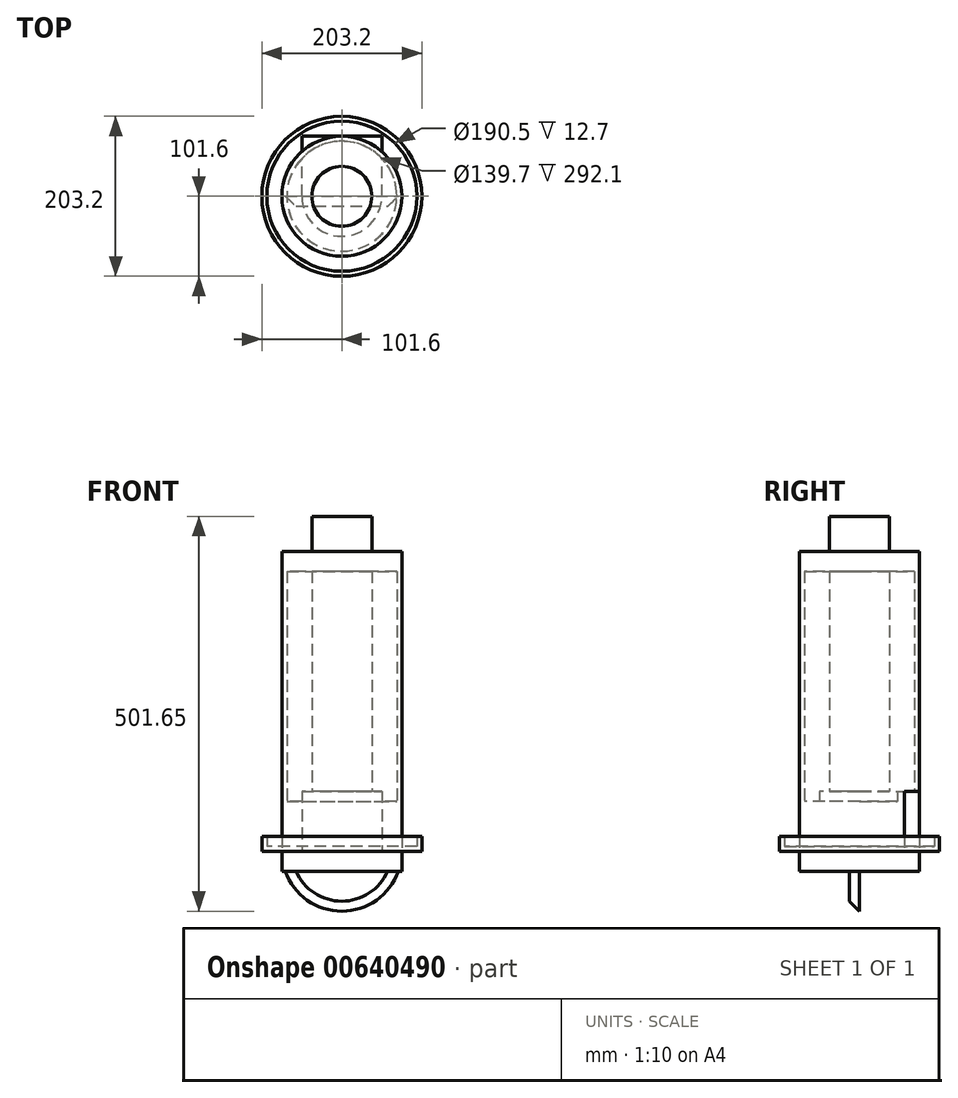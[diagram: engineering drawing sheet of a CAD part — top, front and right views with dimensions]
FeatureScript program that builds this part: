
annotation { "Feature Type Name" : "Feature", "Feature Type Description" : "" }
export const myFeature = defineFeature(function(context is Context, id is Id, definition is map)
    precondition{}
    {
        {
            var Q0;
            Q0=qCreatedBy(makeId("Top.planeOp"),FACE);
            var sketch = newSketch(context, id + "F0", { "sketchPlane" : qUnion([Q0])});
            skArc(sketch, "E0", {"start": v(-50.8, 0) * mm, "mid": v(0, -50.8) * mm, "end": v(50.8, 0) * mm});
            skCircle(sketch, "E1", {"center": v(0, 0) * mm, "radius": 25.4 * mm});
            skLineSegment(sketch, "E2", {"start": v(-50.8, 0) * mm, "end": v(50.8, 0) * mm});
            skLineSegment(sketch, "E3", {"start": v(50.8, 0) * mm, "end": v(50.8, 76.2) * mm});
            skLineSegment(sketch, "E4", {"start": v(-50.8, 0) * mm, "end": v(-50.8, 76.2) * mm});
            skLineSegment(sketch, "E5", {"start": v(-50.8, 76.2) * mm, "end": v(50.8, 76.2) * mm});
            skSolve(sketch);
        }
        {
            var Q0;
            Q0 = qSketchRegion(id + "F0", true);
            extrude(context, id + "F1", {"entities" : qUnion([Q0]), "depth" : 76.2 * mm, "offsetDistance" : 25.4 * mm});
        }
        {
            var Q0;
            Q0=qCreatedBy(makeId("Front.planeOp"),FACE);
            var sketch = newSketch(context, id + "F2", { "sketchPlane" : qUnion([Q0])});
            skCircle(sketch, "E6", {"center": v(0, 0) * mm, "radius": 76.2 * mm});
            skSolve(sketch);
        }
        {
            var Q0;
            Q0 = qSketchRegion(id + "F2", true);
            extrude(context, id + "F3", {"entities" : qUnion([Q0]), "depth" : 12.7 * mm, "offsetDistance" : 25.4 * mm});
        }
        {
            var Q0;
            Q0=makeQuery(id+"F3.opExtrude","CAP_EDGE",EDGE,{"disambiguationData":[OSD([sQuery(id+"F2.wireOp",EDGE,"E6")])],"isStart":false});
            chamfer(context, id + "F4", {"entities" : qUnion([Q0]), "width" : 12.7 * mm, "tangentPropagation" : true});
        }
        {
            var Q0;
            Q0=qCreatedBy(makeId("Top.planeOp"),FACE);
            var sketch = newSketch(context, id + "F5", { "sketchPlane" : qUnion([Q0])});
            skCircle(sketch, "E7", {"center": v(0, 0) * mm, "radius": 76.2 * mm});
            skCircle(sketch, "E8", {"center": v(0, 0) * mm, "radius": 69.85 * mm});
            skSolve(sketch);
        }
        {
            var Q0;
            Q0 = qSketchRegion(id + "F5", true);
            extrude(context, id + "F6", {"entities" : qUnion([Q0]), "depth" : 355.6 * mm, "offsetDistance" : 25.4 * mm});
        }
        {
            var Q0;
            Q0=makeQuery(id+"F6.opExtrude","CAP_FACE",FACE,{"disambiguationData":[OSD([sQuery(id+"F5.wireOp",EDGE,"E7"),sQuery(id+"F5.wireOp",EDGE,"E8")])],"isStart":true});
            var sketch = newSketch(context, id + "F7", { "sketchPlane" : qUnion([Q0])});
            skCircle(sketch, "E9", {"center": v(0, 0) * mm, "radius": 76.2 * mm});
            skSolve(sketch);
        }
        {
            var Q0;
            Q0 = qSketchRegion(id + "F7", true);
            extrude(context, id + "F8", {"entities" : qUnion([Q0]), "operationType" : NewBodyOperationType.ADD, "depth" : 25.4 * mm, "offsetDistance" : 25.4 * mm});
        }
        {
            var Q0;
            Q0=makeQuery(id+"F6.opExtrude","CAP_FACE",FACE,{"disambiguationData":[OSD([sQuery(id+"F5.wireOp",EDGE,"E7"),sQuery(id+"F5.wireOp",EDGE,"E8")])],"isStart":false});
            var sketch = newSketch(context, id + "F9", { "sketchPlane" : qUnion([Q0])});
            skCircle(sketch, "E10", {"center": v(0, 0) * mm, "radius": 76.2 * mm});
            skCircle(sketch, "E11", {"center": v(0, 0) * mm, "radius": 38.1 * mm});
            skSolve(sketch);
        }
        {
            var Q0;
            Q0 = qSketchRegion(id + "F9", true);
            extrude(context, id + "F10", {"entities" : qUnion([Q0]), "operationType" : NewBodyOperationType.ADD, "depth" : 25.4 * mm, "offsetDistance" : 25.4 * mm});
        }
        {
            var Q0;
            Q0=qCreatedBy(makeId("Top.planeOp"),FACE);
            var sketch = newSketch(context, id + "F11", { "sketchPlane" : qUnion([Q0])});
            skCircle(sketch, "E12", {"center": v(0, 0) * mm, "radius": 101.6 * mm});
            skSolve(sketch);
        }
        {
            var Q0;
            Q0 = qSketchRegion(id + "F11", true);
            extrude(context, id + "F12", {"entities" : qUnion([Q0]), "depth" : 6.35 * mm, "offsetDistance" : 25.4 * mm});
        }
        {
            var Q0;
            Q0=makeQuery(id+"F12.opExtrude","CAP_FACE",FACE,{"disambiguationData":[OSD([sQuery(id+"F11.wireOp",EDGE,"E12")])],"isStart":false});
            var sketch = newSketch(context, id + "F13", { "sketchPlane" : qUnion([Q0])});
            skCircle(sketch, "E13", {"center": v(0, 0) * mm, "radius": 101.6 * mm});
            skCircle(sketch, "E14", {"center": v(0, 0) * mm, "radius": 95.25 * mm});
            skSolve(sketch);
        }
        {
            var Q0;
            Q0 = qSketchRegion(id + "F13", true);
            extrude(context, id + "F14", {"entities" : qUnion([Q0]), "operationType" : NewBodyOperationType.ADD, "depth" : 12.7 * mm, "offsetDistance" : 25.4 * mm});
        }
        {
            var Q0;
            Q0=qCreatedBy(makeId("Top.planeOp"),FACE);
            var sketch = newSketch(context, id + "F15", { "sketchPlane" : qUnion([Q0])});
            skCircle(sketch, "E15", {"center": v(0, 0) * mm, "radius": 73.03 * mm});
            skSolve(sketch);
        }
        {
            var Q0;
            Q0 = qSketchRegion(id + "F15", true);
            extrude(context, id + "F16", {"entities" : qUnion([Q0]), "depth" : 63.5 * mm, "offsetDistance" : 25.4 * mm});
        }
        {
            var Q0;
            Q0=makeQuery(id+"F16.opExtrude","CAP_FACE",FACE,{"disambiguationData":[OSD([sQuery(id+"F15.wireOp",EDGE,"E15")])],"isStart":false});
            var sketch = newSketch(context, id + "F17", { "sketchPlane" : qUnion([Q0])});
            skCircle(sketch, "E16", {"center": v(0, 0) * mm, "radius": 38.1 * mm});
            skSolve(sketch);
        }
        {
            var Q0;
            Q0 = qSketchRegion(id + "F17", true);
            extrude(context, id + "F18", {"entities" : qUnion([Q0]), "operationType" : NewBodyOperationType.ADD, "depth" : 361.95 * mm, "offsetDistance" : 25.4 * mm});
        }
    });
